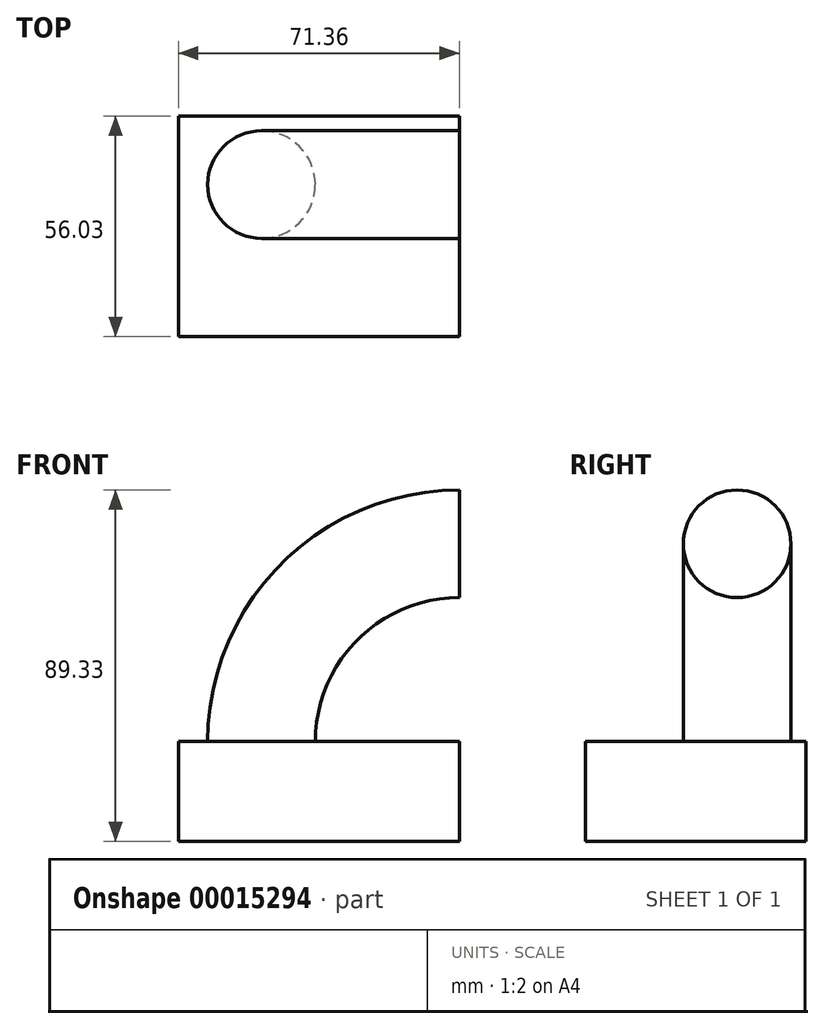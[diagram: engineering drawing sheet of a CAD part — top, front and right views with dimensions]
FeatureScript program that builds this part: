
annotation { "Feature Type Name" : "Feature", "Feature Type Description" : "" }
export const myFeature = defineFeature(function(context is Context, id is Id, definition is map)
    precondition{}
    {
        {
            var Q0;
            Q0=qCreatedBy(makeId("Top.planeOp"),FACE);
            var sketch = newSketch(context, id + "F0", { "sketchPlane" : qUnion([Q0])});
            skLineSegment(sketch, "E0.bottom", {"start": v(-49.14, 26.92) * mm, "end": v(22.22, 26.92) * mm});
            skLineSegment(sketch, "E0.top", {"start": v(-49.14, -29.1) * mm, "end": v(22.22, -29.1) * mm});
            skLineSegment(sketch, "E0.left", {"start": v(-49.14, 26.92) * mm, "end": v(-49.14, -29.1) * mm});
            skLineSegment(sketch, "E0.right", {"start": v(22.22, 26.92) * mm, "end": v(22.22, -29.1) * mm});
            skSolve(sketch);
        }
        {
            var Q0;
            Q0=makeQuery(id+"F0.imprint","IMPRINT",FACE,{"disambiguationData":[TD([[makeQuery(id+"F0.imprint","IMPRINT",EDGE,{"derivedFrom":sQuery(id+"F0.wireOp",EDGE,"E0.bottom")}),-1.0]])]});
            extrude(context, id + "F1", {"entities" : qUnion([Q0]), "depth" : 25.4 * mm});
        }
        {
            var Q0;
            Q0=makeQuery(id+"F1.opExtrude","CAP_FACE",FACE,{"disambiguationData":[OSD([sQuery(id+"F0.wireOp",EDGE,"E0.bottom"),sQuery(id+"F0.wireOp",EDGE,"E0.top"),sQuery(id+"F0.wireOp",EDGE,"E0.left"),sQuery(id+"F0.wireOp",EDGE,"E0.right")])],"isStart":false});
            var sketch = newSketch(context, id + "F2", { "sketchPlane" : qUnion([Q0])});
            skCircle(sketch, "E1", {"center": v(-28.04, 9.48) * mm, "radius": 13.67 * mm});
            skSolve(sketch);
        }
        {
            var Q0;
            Q0=makeQuery(id+"F2.imprint","IMPRINT",FACE,{"disambiguationData":[TD([[makeQuery(id+"F2.imprint","IMPRINT",EDGE,{"derivedFrom":sQuery(id+"F2.wireOp",EDGE,"E1")}),1.0]])]});
            var Q1;
            Q1=makeQuery(id+"F1.opExtrude","CAP_EDGE",EDGE,{"disambiguationData":[OSD([sQuery(id+"F0.wireOp",EDGE,"E0.right")])],"isStart":false});
            revolve(context, id + "F3", {"operationType" : NewBodyOperationType.ADD, "entities" : qUnion([Q0]), "axis" : qUnion([Q1]), "revolveType" : RevolveType.ONE_DIRECTION, "oppositeDirection" : true, "angle" : 90 * degree});
        }
    });
